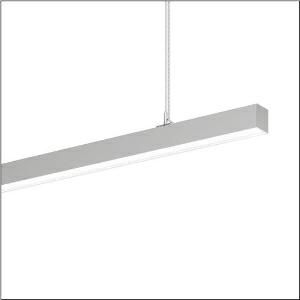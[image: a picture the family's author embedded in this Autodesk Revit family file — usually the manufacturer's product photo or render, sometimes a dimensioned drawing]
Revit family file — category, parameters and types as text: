
# Revit family: silica_r__21_51mx30dc39sb_d950
name_source: partatom
category: Lighting Fixtures
units: mm (PartAtom-declared; Revit-internal decimal feet)

## family parameters
Cut with Voids When Loaded = No
Host = Face
Light Source = No
Part Type = Normal
Room Calculation Point = No
Round Connector Dimension = Use Diameter
Shared = No

## types (1)
- --- (1 x LED, 10520 lm, 68.3 W, 3000K)
    Apparent Load = 68 VA
    CIE Flux Codes = 47 79 96 57 100
    Color Rendering = 80
    Color Temperature = 3000K
    Default Elevation = 1800 mm
    Description = Silica® 21, office luminaire, primary optical cover: cover, of PMMA, opal, light emission: direct/indirect distribution, primary light characteristic: symmetric, installation type: suspended mounting, LED, rated luminous flux: 10.520lm, luminous efficacy: 154lm/W, light colour: 830, colour temperature: 3000K, with terminal, 3+2-pole, max. 2.5mm², mains connection: 220..240V, AC, 50/60Hz, rated input power: 68.3W, luminaire housing, of aluminium, metallic grey (RAL 9006), length: 3.004mm, width: 53mm, height: 53mm, protection rating (complete): IP20, insulation class (complete): insulation class I (protective earthing), certification: CE, permissible operating ambient temperature: 0..+35°C, standard: EN 50419, packaging unit: 1 piece
    Height = 53 mm
    Lamp = 1 x LED
    Lamp Light Flux = 10520 lm
    Lamp Power = 68.3 W
    Lamp count = 1
    Length = 3004 mm
    Luminous efficacy = 154 lm/W
    Manufacturer = Siteco
    ModVariant = No
    Model = 51MX30DC39SB
    Mounting Place = Ceiling
    Mounting Type = Pendant
    Number of Poles = 1
    OnlyDefault = Yes
    Power Factor = 1
    Product Name = Silica® 21
    Product group = office luminaire | ceiling pendant
    ProductGroupID = 902
    Protection Class = Protection class I
    Protection Degree = IP 20
    RLX_Detail_Level = 1
    RLX_Emergency_Light_Flux = 0 lm
    RLX_Emergency_Type = 0
    RLX_Emergency_Type_DB = No
    RlxData = <blob elided: 23349 chars, md5=f6abdf7e>
    Socket = socket
    Standby Power = 0 W
    System Light Flux = 10520 lm
    System Power = 68 W
    Type Comments = factory setting: luminous flux: 100 % | dim-lin: 254 | 233 mA
    Type Image = l_1335864.jpg
    URL = http://relux.com
    VarID = @adj_085909
    Voltage = 0 V
    Weight = 0.00 kg
    Width = 53 mm

## geometry (parser evidence)
native form markers: Blend x4, Sweep x14
no freeform markers — native parametric forms only
